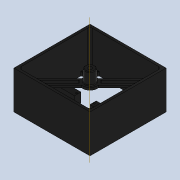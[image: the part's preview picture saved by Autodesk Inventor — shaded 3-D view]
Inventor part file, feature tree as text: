
AUTODESK INVENTOR PART (.ipt)
format: ipt  version: 2022 (Build 260153000, 153)  size: 308,736 bytes
history: native  units: in
note: dims shown in document units (in); Inventor stores cm internally (conversion verified against a paired STEP export)
features: extrude x7, sketch x6, chamfer x2, pattern_circular x1, fillet x1, plane x1, projected_geometry x1
ambient origin geometry x8: Origin, YZ Plane, XZ Plane, XY Plane, X Axis, Y Axis, Z Axis, Center Point
bodies: Solid1 (feature_tree)
feature tree (19):
  sketch  "Sketch1"  dims[d0=4.0in d1=4.0in]
  extrude  "Extrusion1"  Depth=4.0in
  extrude  "Extrusion2"  Depth=0.125in
  pattern_circular  "Circular Pattern1"  Count=4 Angle=360.0deg
  chamfer  "Chamfer4"  Distance=0.125in Angle=45.0deg
  extrude  "Extrusion3"  Depth=0.34in
  extrude  "Extrusion4"  Depth=1.717in
  extrude  "Extrusion5"  Depth=0.34in
  extrude  "Extrusion6"  Depth=0.375in
  chamfer  "Chamfer5"  Distance=0.066in
  fillet  "Fillet1"  Radius=0.08in
  extrude  "Extrusion7"  Depth=0.375in
  plane  "Work Plane1"
  sketch  "Sketch2"  dims[d2=0.125in d3=0.201in]
  projected_geometry  "Projected Loop1"
  sketch  "Sketch3"  dims[d4=0.125in]
  sketch  "Sketch4"  dims[d5=1.25in d6=0.0in]
  sketch  "Sketch5"  dims[d7=0.1875in d8=0.0in d18=1.5748in d19=360.0deg d21=0.0312in d22=0.125in d23=45.0deg]
  sketch  "Sketch6"  dims[d24=1.232in d25=0.34in d26=1.717in d27=0.34in d28=0.08in d29=0.066in d30=0.08in d31=0.066in d32=0.5in d33=0.0in d34=0.095in d35=0.095in d36=0.125in d37=0.125in d38=0.125in d39=0.0in d40=0.125in d41=0.625in d42=0.0in d44=0.75in d46=0.5in d47=0.125in d48=0.0in d49=0.0312in d50=0.125in d51=45.0deg d52=0.0625in d53=0.125in d54=0.208in d55=0.375in d56=0.0in]
